# Revit family: MADEL_DAMPER_AIR VOLUME CONTROL_SQR_tarifa
name_source: partatom
category: Accesorios de conductos
revit_build: Autodesk Revit 2015 (Build: 20140606_1530(x64)
units: mm (PartAtom-declared; Revit-internal decimal feet)

## types (230) — shared parameters
BIMETRICAL = http://www.bimetrical.com
BIMETRICAL Category = Damper
Comentarios de tipo = The SQR series damper are designed to be used for altering the flow volume rate and pressure in air-conditioning, ventilation and heating systems. Opposed blades of 100 mm.
Descripción = MADEL_Air volume dampers for rectangular ducts
Fabricante = MADEL
Family Version = 1.0
IfcExportAs = IfcDamperType
IfcExportType = IfcDamperType
Imagen de tipo = <Ninguno>
Material Damper = <Por categoría>
Review Date = 11/2016
Revit Version = Revit 2015 - English
URL = http://www.madel.com
Vmax = 7.0 m/s
Vmed = 4.0 m/s
Vmin = 1.0 m/s
b_factor = -0.69
c_factor = -6.9395
m_factor = 2.16
n_factor = 28.867

## per-type parameters (varying)
| type | Afree | H | L | Modelo | Nº  Blades | Product Size | Q max | Q min |
| SQR-EH 2000x1000 | 1.9603 m² | 1000 mm  [stored 3.28084 ft] | 2000 mm  [stored 6.56168 ft] | SQR-EH 2000x1000 | 20 | 2000x1000 | 49,398 m³/h | 7,057 m³/h |
| SQR-EH 2000x900 | 1.7642 m² | 900 mm  [stored 2.95276 ft] | 2000 mm  [stored 6.56168 ft] | SQR-EH 2000x900 | 18 | 2000x900 | 44,458 m³/h | 6,351 m³/h |
| SQR-EH 2000x800 | 1.5682 m² | 800 mm  [stored 2.62467 ft] | 2000 mm  [stored 6.56168 ft] | SQR-EH 2000x800 | 16 | 2000x800 | 39,519 m³/h | 5,646 m³/h |
| SQR-EH 2000x700 | 1.3722 m² | 700 mm  [stored 2.29659 ft] | 2000 mm  [stored 6.56168 ft] | SQR-EH 2000x700 | 14 | 2000x700 | 34,579 m³/h | 4,940 m³/h |
| SQR-EH 2000x600 | 1.1762 m² | 600 mm | 2000 mm  [stored 6.56168 ft] | SQR-EH 2000x600 | 12 | 2000x600 | 29,639 m³/h | 4,234 m³/h |
| SQR-EH 2000x500 | 0.9801 m² | 500 mm  [stored 1.64042 ft] | 2000 mm  [stored 6.56168 ft] | SQR-EH 2000x500 | 10 | 2000x500 | 24,699 m³/h | 3,528 m³/h |
| SQR-EH 2000x400 | 0.7841 m² | 400 mm  [stored 1.31234 ft] | 2000 mm  [stored 6.56168 ft] | SQR-EH 2000x400 | 8 | 2000x400 | 19,759 m³/h | 2,823 m³/h |
| SQR-EH 2000x300 | 0.5881 m² | 300 mm | 2000 mm  [stored 6.56168 ft] | SQR-EH 2000x300 | 6 | 2000x300 | 14,819 m³/h | 2,117 m³/h |
| SQR-EH 2000x250 | 0.4921 m² | 250 mm  [stored 0.82021 ft] | 2000 mm  [stored 6.56168 ft] | SQR-EH 2000x250 | 4 | 2000x250 | 12,400 m³/h | 1,771 m³/h |
| SQR-EH 2000x200 | 0.3921 m² | 200 mm  [stored 0.656168 ft] | 2000 mm  [stored 6.56168 ft] | SQR-EH 2000x200 | 4 | 2000x200 | 9,880 m³/h | 1,411 m³/h |
| SQR-EH 2000x150 | 0.2960 m² | 150 mm | 2000 mm  [stored 6.56168 ft] | SQR-EH 2000x150 | 2 | 2000x150 | 7,460 m³/h | 1,066 m³/h |
| SQR-EH 2000x100 | 0.1960 m² | 100 mm  [stored 0.328084 ft] | 2000 mm  [stored 6.56168 ft] | SQR-EH 2000x100 | 2 | 2000x100 | 4,940 m³/h | 706 m³/h |
| SQR-EH 1800x1000 | 1.7643 m² | 1000 mm  [stored 3.28084 ft] | 1800 mm | SQR-EH 1800x1000 | 20 | 1800x1000 | 44,459 m³/h | 6,351 m³/h |
| SQR-EH 1800x900 | 1.5878 m² | 900 mm  [stored 2.95276 ft] | 1800 mm | SQR-EH 1800x900 | 18 | 1800x900 | 40,013 m³/h | 5,716 m³/h |
| SQR-EH 1800x800 | 1.4114 m² | 800 mm  [stored 2.62467 ft] | 1800 mm | SQR-EH 1800x800 | 16 | 1800x800 | 35,567 m³/h | 5,081 m³/h |
| SQR-EH 1800x700 | 1.2350 m² | 700 mm  [stored 2.29659 ft] | 1800 mm | SQR-EH 1800x700 | 14 | 1800x700 | 31,121 m³/h | 4,446 m³/h |
| SQR-EH 1800x600 | 1.0586 m² | 600 mm | 1800 mm | SQR-EH 1800x600 | 12 | 1800x600 | 26,675 m³/h | 3,811 m³/h |
| SQR-EH 1800x500 | 0.8821 m² | 500 mm  [stored 1.64042 ft] | 1800 mm | SQR-EH 1800x500 | 10 | 1800x500 | 22,230 m³/h | 3,176 m³/h |
| SQR-EH 1800x400 | 0.7057 m² | 400 mm  [stored 1.31234 ft] | 1800 mm | SQR-EH 1800x400 | 8 | 1800x400 | 17,784 m³/h | 2,541 m³/h |
| SQR-EH 1800x300 | 0.5293 m² | 300 mm | 1800 mm | SQR-EH 1800x300 | 6 | 1800x300 | 13,338 m³/h | 1,905 m³/h |
| SQR-EH 1800x250 | 0.4429 m² | 250 mm  [stored 0.82021 ft] | 1800 mm | SQR-EH 1800x250 | 4 | 1800x250 | 11,160 m³/h | 1,594 m³/h |
| SQR-EH 1800x200 | 0.3529 m² | 200 mm  [stored 0.656168 ft] | 1800 mm | SQR-EH 1800x200 | 4 | 1800x200 | 8,892 m³/h | 1,270 m³/h |
| SQR-EH 1800x150 | 0.2664 m² | 150 mm | 1800 mm | SQR-EH 1800x150 | 2 | 1800x150 | 6,714 m³/h | 959 m³/h |
| SQR-EH 1800x100 | 0.1764 m² | 100 mm  [stored 0.328084 ft] | 1800 mm | SQR-EH 1800x100 | 2 | 1800x100 | 4,446 m³/h | 635 m³/h |
| SQR-EH 1600x1000 | 1.5683 m² | 1000 mm  [stored 3.28084 ft] | 1600 mm | SQR-EH 1600x1000 | 20 | 1600x1000 | 39,520 m³/h | 5,646 m³/h |
| SQR-EH 1600x900 | 1.4114 m² | 900 mm  [stored 2.95276 ft] | 1600 mm | SQR-EH 1600x900 | 18 | 1600x900 | 35,568 m³/h | 5,081 m³/h |
| SQR-EH 1600x800 | 1.2546 m² | 800 mm  [stored 2.62467 ft] | 1600 mm | SQR-EH 1600x800 | 16 | 1600x800 | 31,616 m³/h | 4,517 m³/h |
| SQR-EH 1600x700 | 1.0978 m² | 700 mm  [stored 2.29659 ft] | 1600 mm | SQR-EH 1600x700 | 14 | 1600x700 | 27,664 m³/h | 3,952 m³/h |
| SQR-EH 1600x600 | 0.9410 m² | 600 mm | 1600 mm | SQR-EH 1600x600 | 12 | 1600x600 | 23,712 m³/h | 3,387 m³/h |
| SQR-EH 1600x500 | 0.7841 m² | 500 mm  [stored 1.64042 ft] | 1600 mm | SQR-EH 1600x500 | 10 | 1600x500 | 19,760 m³/h | 2,823 m³/h |
| SQR-EH 1600x400 | 0.6273 m² | 400 mm  [stored 1.31234 ft] | 1600 mm | SQR-EH 1600x400 | 8 | 1600x400 | 15,808 m³/h | 2,258 m³/h |
| SQR-EH 1600x300 | 0.4705 m² | 300 mm | 1600 mm | SQR-EH 1600x300 | 6 | 1600x300 | 11,856 m³/h | 1,694 m³/h |
| SQR-EH 1600x250 | 0.3937 m² | 250 mm  [stored 0.82021 ft] | 1600 mm | SQR-EH 1600x250 | 4 | 1600x250 | 9,920 m³/h | 1,417 m³/h |
| SQR-EH 1600x200 | 0.3137 m² | 200 mm  [stored 0.656168 ft] | 1600 mm | SQR-EH 1600x200 | 4 | 1600x200 | 7,904 m³/h | 1,129 m³/h |
| SQR-EH 1600x150 | 0.2368 m² | 150 mm | 1600 mm | SQR-EH 1600x150 | 2 | 1600x150 | 5,968 m³/h | 853 m³/h |
| SQR-EH 1600x100 | 0.1568 m² | 100 mm  [stored 0.328084 ft] | 1600 mm | SQR-EH 1600x100 | 2 | 1600x100 | 3,952 m³/h | 565 m³/h |
| SQR-EH 1400x1000 | 1.3723 m² | 1000 mm  [stored 3.28084 ft] | 1400 mm  [stored 4.59318 ft] | SQR-EH 1400x1000 | 20 | 1400x1000 | 34,581 m³/h | 4,940 m³/h |
| SQR-EH 1400x900 | 1.2350 m² | 900 mm  [stored 2.95276 ft] | 1400 mm  [stored 4.59318 ft] | SQR-EH 1400x900 | 18 | 1400x900 | 31,123 m³/h | 4,446 m³/h |
| SQR-EH 1400x800 | 1.0978 m² | 800 mm  [stored 2.62467 ft] | 1400 mm  [stored 4.59318 ft] | SQR-EH 1400x800 | 16 | 1400x800 | 27,665 m³/h | 3,952 m³/h |
| SQR-EH 1400x700 | 0.9606 m² | 700 mm  [stored 2.29659 ft] | 1400 mm  [stored 4.59318 ft] | SQR-EH 1400x700 | 14 | 1400x700 | 24,206 m³/h | 3,458 m³/h |
| SQR-EH 1400x600 | 0.8234 m² | 600 mm | 1400 mm  [stored 4.59318 ft] | SQR-EH 1400x600 | 12 | 1400x600 | 20,748 m³/h | 2,964 m³/h |
| SQR-EH 1400x500 | 0.6861 m² | 500 mm  [stored 1.64042 ft] | 1400 mm  [stored 4.59318 ft] | SQR-EH 1400x500 | 10 | 1400x500 | 17,290 m³/h | 2,470 m³/h |
| SQR-EH 1400x400 | 0.5489 m² | 400 mm  [stored 1.31234 ft] | 1400 mm  [stored 4.59318 ft] | SQR-EH 1400x400 | 8 | 1400x400 | 13,832 m³/h | 1,976 m³/h |
| SQR-EH 1400x300 | 0.4117 m² | 300 mm | 1400 mm  [stored 4.59318 ft] | SQR-EH 1400x300 | 6 | 1400x300 | 10,374 m³/h | 1,482 m³/h |
| SQR-EH 1400x250 | 0.3445 m² | 250 mm  [stored 0.82021 ft] | 1400 mm  [stored 4.59318 ft] | SQR-EH 1400x250 | 4 | 1400x250 | 8,680 m³/h | 1,240 m³/h |
| SQR-EH 1400x200 | 0.2745 m² | 200 mm  [stored 0.656168 ft] | 1400 mm  [stored 4.59318 ft] | SQR-EH 1400x200 | 4 | 1400x200 | 6,916 m³/h | 988 m³/h |
| SQR-EH 1400x150 | 0.2072 m² | 150 mm | 1400 mm  [stored 4.59318 ft] | SQR-EH 1400x150 | 2 | 1400x150 | 5,222 m³/h | 746 m³/h |
| SQR-EH 1400x100 | 0.1372 m² | 100 mm  [stored 0.328084 ft] | 1400 mm  [stored 4.59318 ft] | SQR-EH 1400x100 | 2 | 1400x100 | 3,458 m³/h | 494 m³/h |
| SQR-EH 1200x1000 | 1.1881 m² | 1000 mm  [stored 3.28084 ft] | 1200 mm | SQR-EH 1200x1000 | 10 | 1200x1000 | 29,941 m³/h | 4,277 m³/h |
| SQR-EH 1200x900 | 1.0693 m² | 900 mm  [stored 2.95276 ft] | 1200 mm | SQR-EH 1200x900 | 9 | 1200x900 | 26,947 m³/h | 3,850 m³/h |
| SQR-EH 1200x800 | 0.9505 m² | 800 mm  [stored 2.62467 ft] | 1200 mm | SQR-EH 1200x800 | 8 | 1200x800 | 23,953 m³/h | 3,422 m³/h |
| SQR-EH 1200x700 | 0.8317 m² | 700 mm  [stored 2.29659 ft] | 1200 mm | SQR-EH 1200x700 | 7 | 1200x700 | 20,959 m³/h | 2,994 m³/h |
| SQR-EH 1200x600 | 0.7129 m² | 600 mm | 1200 mm | SQR-EH 1200x600 | 6 | 1200x600 | 17,964 m³/h | 2,566 m³/h |
| SQR-EH 1200x500 | 0.5941 m² | 500 mm  [stored 1.64042 ft] | 1200 mm | SQR-EH 1200x500 | 5 | 1200x500 | 14,970 m³/h | 2,139 m³/h |
| SQR-EH 1200x400 | 0.4753 m² | 400 mm  [stored 1.31234 ft] | 1200 mm | SQR-EH 1200x400 | 4 | 1200x400 | 11,976 m³/h | 1,711 m³/h |
| SQR-EH 1200x300 | 0.3564 m² | 300 mm | 1200 mm | SQR-EH 1200x300 | 3 | 1200x300 | 8,982 m³/h | 1,283 m³/h |
| SQR-EH 1200x250 | 0.2976 m² | 250 mm  [stored 0.82021 ft] | 1200 mm | SQR-EH 1200x250 | 2 | 1200x250 | 7,500 m³/h | 1,071 m³/h |
| SQR-EH 1200x200 | 0.2376 m² | 200 mm  [stored 0.656168 ft] | 1200 mm | SQR-EH 1200x200 | 2 | 1200x200 | 5,988 m³/h | 855 m³/h |
| SQR-EH 1200x150 | 0.1788 m² | 150 mm | 1200 mm | SQR-EH 1200x150 | 1 | 1200x150 | 4,506 m³/h | 644 m³/h |
| SQR-EH 1200x100 | 0.1188 m² | 100 mm  [stored 0.328084 ft] | 1200 mm | SQR-EH 1200x100 | 1 | 1200x100 | 2,994 m³/h | 428 m³/h |
| SQR-EH 1100x1000 | 1.0891 m² | 1000 mm  [stored 3.28084 ft] | 1100 mm | SQR-EH 1100x1000 | 10 | 1100x1000 | 27,446 m³/h | 3,921 m³/h |
| SQR-EH 1100x900 | 0.9802 m² | 900 mm  [stored 2.95276 ft] | 1100 mm | SQR-EH 1100x900 | 9 | 1100x900 | 24,701 m³/h | 3,529 m³/h |
| SQR-EH 1100x800 | 0.8713 m² | 800 mm  [stored 2.62467 ft] | 1100 mm | SQR-EH 1100x800 | 8 | 1100x800 | 21,957 m³/h | 3,137 m³/h |
| SQR-EH 1100x700 | 0.7624 m² | 700 mm  [stored 2.29659 ft] | 1100 mm | SQR-EH 1100x700 | 7 | 1100x700 | 19,212 m³/h | 2,745 m³/h |
| SQR-EH 1100x600 | 0.6535 m² | 600 mm | 1100 mm | SQR-EH 1100x600 | 6 | 1100x600 | 16,468 m³/h | 2,353 m³/h |
| SQR-EH 1100x500 | 0.5446 m² | 500 mm  [stored 1.64042 ft] | 1100 mm | SQR-EH 1100x500 | 5 | 1100x500 | 13,723 m³/h | 1,960 m³/h |
| SQR-EH 1100x400 | 0.4357 m² | 400 mm  [stored 1.31234 ft] | 1100 mm | SQR-EH 1100x400 | 4 | 1100x400 | 10,978 m³/h | 1,568 m³/h |
| SQR-EH 1100x300 | 0.3267 m² | 300 mm | 1100 mm | SQR-EH 1100x300 | 3 | 1100x300 | 8,234 m³/h | 1,176 m³/h |
| SQR-EH 1100x250 | 0.2728 m² | 250 mm  [stored 0.82021 ft] | 1100 mm | SQR-EH 1100x250 | 2 | 1100x250 | 6,875 m³/h | 982 m³/h |
| SQR-EH 1100x200 | 0.2178 m² | 200 mm  [stored 0.656168 ft] | 1100 mm | SQR-EH 1100x200 | 2 | 1100x200 | 5,489 m³/h | 784 m³/h |
| SQR-EH 1100x150 | 0.1639 m² | 150 mm | 1100 mm | SQR-EH 1100x150 | 1 | 1100x150 | 4,131 m³/h | 590 m³/h |
| SQR-EH 1100x100 | 0.1089 m² | 100 mm  [stored 0.328084 ft] | 1100 mm | SQR-EH 1100x100 | 1 | 1100x100 | 2,745 m³/h | 392 m³/h |
| SQR-EH 1000x1000 | 0.9901 m² | 1000 mm  [stored 3.28084 ft] | 1000 mm  [stored 3.28084 ft] | SQR-EH 1000x1000 | 10 | 1000x1000 | 24,951 m³/h | 3,564 m³/h |
| SQR-EH 1000x900 | 0.8911 m² | 900 mm  [stored 2.95276 ft] | 1000 mm  [stored 3.28084 ft] | SQR-EH 1000x900 | 9 | 1000x900 | 22,456 m³/h | 3,208 m³/h |
| SQR-EH 1000x800 | 0.7921 m² | 800 mm  [stored 2.62467 ft] | 1000 mm  [stored 3.28084 ft] | SQR-EH 1000x800 | 8 | 1000x800 | 19,961 m³/h | 2,852 m³/h |
| SQR-EH 1000x700 | 0.6931 m² | 700 mm  [stored 2.29659 ft] | 1000 mm  [stored 3.28084 ft] | SQR-EH 1000x700 | 7 | 1000x700 | 17,466 m³/h | 2,495 m³/h |
| SQR-EH 1000x600 | 0.5941 m² | 600 mm | 1000 mm  [stored 3.28084 ft] | SQR-EH 1000x600 | 6 | 1000x600 | 14,971 m³/h | 2,139 m³/h |
| SQR-EH 1000x500 | 0.4951 m² | 500 mm  [stored 1.64042 ft] | 1000 mm  [stored 3.28084 ft] | SQR-EH 1000x500 | 5 | 1000x500 | 12,476 m³/h | 1,782 m³/h |
| SQR-EH 1000x400 | 0.3961 m² | 400 mm  [stored 1.31234 ft] | 1000 mm  [stored 3.28084 ft] | SQR-EH 1000x400 | 4 | 1000x400 | 9,980 m³/h | 1,426 m³/h |
| SQR-EH 1000x300 | 0.2970 m² | 300 mm | 1000 mm  [stored 3.28084 ft] | SQR-EH 1000x300 | 3 | 1000x300 | 7,485 m³/h | 1,069 m³/h |
| SQR-EH 1000x250 | 0.2480 m² | 250 mm  [stored 0.82021 ft] | 1000 mm  [stored 3.28084 ft] | SQR-EH 1000x250 | 2 | 1000x250 | 6,250 m³/h | 893 m³/h |
| SQR-EH 1000x200 | 0.1980 m² | 200 mm  [stored 0.656168 ft] | 1000 mm  [stored 3.28084 ft] | SQR-EH 1000x200 | 2 | 1000x200 | 4,990 m³/h | 713 m³/h |
| SQR-EH 1000x150 | 0.1490 m² | 150 mm | 1000 mm  [stored 3.28084 ft] | SQR-EH 1000x150 | 1 | 1000x150 | 3,755 m³/h | 536 m³/h |
| SQR-EH 1000x100 | 0.0990 m² | 100 mm  [stored 0.328084 ft] | 1000 mm  [stored 3.28084 ft] | SQR-EH 1000x100 | 1 | 1000x100 | 2,495 m³/h | 356 m³/h |
| SQR-EV 1000x900 | 0.8911 m² | 1000 mm  [stored 3.28084 ft] | 900 mm  [stored 2.95276 ft] | SQR-EV 1000x900 | 10 | 900x1000 | 22,456 m³/h | 3,208 m³/h |
| SQR-EH 900x900 | 0.8020 m² | 900 mm  [stored 2.95276 ft] | 900 mm  [stored 2.95276 ft] | SQR-EH 900x900 | 9 | 900x900 | 20,211 m³/h | 2,887 m³/h |
| SQR-EH 900x800 | 0.7129 m² | 800 mm  [stored 2.62467 ft] | 900 mm  [stored 2.95276 ft] | SQR-EH 900x800 | 8 | 900x800 | 17,965 m³/h | 2,566 m³/h |
| SQR-EH 900x700 | 0.6238 m² | 700 mm  [stored 2.29659 ft] | 900 mm  [stored 2.95276 ft] | SQR-EH 900x700 | 7 | 900x700 | 15,719 m³/h | 2,246 m³/h |
| SQR-EH 900x500 | 0.4456 m² | 500 mm  [stored 1.64042 ft] | 900 mm  [stored 2.95276 ft] | SQR-EH 900x500 | 5 | 900x500 | 11,228 m³/h | 1,604 m³/h |
| SQR-EH 900x400 | 0.3565 m² | 400 mm  [stored 1.31234 ft] | 900 mm  [stored 2.95276 ft] | SQR-EH 900x400 | 4 | 900x400 | 8,983 m³/h | 1,283 m³/h |
| SQR-EH 900x300 | 0.2673 m² | 300 mm | 900 mm  [stored 2.95276 ft] | SQR-EH 900x300 | 3 | 900x300 | 6,737 m³/h | 962 m³/h |
| SQR-EH 900x250 | 0.2232 m² | 250 mm  [stored 0.82021 ft] | 900 mm  [stored 2.95276 ft] | SQR-EH 900x250 | 2 | 900x250 | 5,625 m³/h | 804 m³/h |
| SQR-EH 900x200 | 0.1782 m² | 200 mm  [stored 0.656168 ft] | 900 mm  [stored 2.95276 ft] | SQR-EH 900x200 | 2 | 900x200 | 4,491 m³/h | 642 m³/h |
| SQR-EH 900x150 | 0.1341 m² | 150 mm | 900 mm  [stored 2.95276 ft] | SQR-EH 900x150 | 1 | 900x150 | 3,380 m³/h | 483 m³/h |
| SQR-EH 900x100 | 0.0891 m² | 100 mm  [stored 0.328084 ft] | 900 mm  [stored 2.95276 ft] | SQR-EH 900x100 | 1 | 900x100 | 2,246 m³/h | 321 m³/h |
| SQR-EV 1000x800 | 0.7921 m² | 1000 mm  [stored 3.28084 ft] | 800 mm  [stored 2.62467 ft] | SQR-EV 1000x800 | 10 | 800x1000 | 19,962 m³/h | 2,852 m³/h |
| SQR-EV 900x800 | 0.7129 m² | 900 mm  [stored 2.95276 ft] | 800 mm  [stored 2.62467 ft] | SQR-EV 900x800 | 9 | 800x900 | 17,965 m³/h | 2,566 m³/h |
| SQR-EV 850x800 | 0.6737 m² | 850 mm  [stored 2.78871 ft] | 800 mm  [stored 2.62467 ft] | SQR-EV 850x800 | 8 | 800x850 | 16,977 m³/h | 2,425 m³/h |
| SQR-EH 800x800 | 0.6337 m² | 800 mm  [stored 2.62467 ft] | 800 mm  [stored 2.62467 ft] | SQR-EH 800x800 | 8 | 800x800 | 15,969 m³/h | 2,281 m³/h |
| SQR-EH 800x700 | 0.5545 m² | 700 mm  [stored 2.29659 ft] | 800 mm  [stored 2.62467 ft] | SQR-EH 800x700 | 7 | 800x700 | 13,973 m³/h | 1,996 m³/h |
| SQR-EH 800x600 | 0.4753 m² | 600 mm | 800 mm  [stored 2.62467 ft] | SQR-EH 800x600 | 6 | 800x600 | 11,977 m³/h | 1,711 m³/h |
| SQR-EH 800x500 | 0.3961 m² | 500 mm  [stored 1.64042 ft] | 800 mm  [stored 2.62467 ft] | SQR-EH 800x500 | 5 | 800x500 | 9,981 m³/h | 1,426 m³/h |
| SQR-EH 800x400 | 0.3169 m² | 400 mm  [stored 1.31234 ft] | 800 mm  [stored 2.62467 ft] | SQR-EH 800x400 | 4 | 800x400 | 7,985 m³/h | 1,141 m³/h |
| SQR-EH 800x300 | 0.2376 m² | 300 mm | 800 mm  [stored 2.62467 ft] | SQR-EH 800x300 | 3 | 800x300 | 5,988 m³/h | 855 m³/h |
| SQR-EH 800x250 | 0.1984 m² | 250 mm  [stored 0.82021 ft] | 800 mm  [stored 2.62467 ft] | SQR-EH 800x250 | 2 | 800x250 | 5,000 m³/h | 714 m³/h |
| SQR-EH 800x200 | 0.1584 m² | 200 mm  [stored 0.656168 ft] | 800 mm  [stored 2.62467 ft] | SQR-EH 800x200 | 2 | 800x200 | 3,992 m³/h | 570 m³/h |
| SQR-EH 800x150 | 0.1192 m² | 150 mm | 800 mm  [stored 2.62467 ft] | SQR-EH 800x150 | 1 | 800x150 | 3,004 m³/h | 429 m³/h |
| SQR-EH 800x100 | 0.0792 m² | 100 mm  [stored 0.328084 ft] | 800 mm  [stored 2.62467 ft] | SQR-EH 800x100 | 1 | 800x100 | 1,996 m³/h | 285 m³/h |
| SQR-EH 700x700 | 0.4852 m² | 700 mm  [stored 2.29659 ft] | 700 mm  [stored 2.29659 ft] | SQR-EH 700x700 | 7 | 700x700 | 12,227 m³/h | 1,747 m³/h |
| SQR-EH 700x600 | 0.4159 m² | 600 mm | 700 mm  [stored 2.29659 ft] | SQR-EH 700x600 | 6 | 700x600 | 10,480 m³/h | 1,497 m³/h |
| SQR-EH 700x500 | 0.3466 m² | 500 mm  [stored 1.64042 ft] | 700 mm  [stored 2.29659 ft] | SQR-EH 700x500 | 5 | 700x500 | 8,733 m³/h | 1,248 m³/h |
| SQR-EH 700x400 | 0.2773 m² | 400 mm  [stored 1.31234 ft] | 700 mm  [stored 2.29659 ft] | SQR-EH 700x400 | 4 | 700x400 | 6,987 m³/h | 998 m³/h |
| SQR-EH 700x300 | 0.2079 m² | 300 mm | 700 mm  [stored 2.29659 ft] | SQR-EH 700x300 | 3 | 700x300 | 5,240 m³/h | 749 m³/h |
| SQR-EH 700x250 | 0.1736 m² | 250 mm  [stored 0.82021 ft] | 700 mm  [stored 2.29659 ft] | SQR-EH 700x250 | 2 | 700x250 | 4,375 m³/h | 625 m³/h |
| SQR-EH 700x200 | 0.1386 m² | 200 mm  [stored 0.656168 ft] | 700 mm  [stored 2.29659 ft] | SQR-EH 700x200 | 2 | 700x200 | 3,493 m³/h | 499 m³/h |
| SQR-EH 700x150 | 0.1043 m² | 150 mm | 700 mm  [stored 2.29659 ft] | SQR-EH 700x150 | 1 | 700x150 | 2,629 m³/h | 376 m³/h |
| SQR-EH 700x100 | 0.0693 m² | 100 mm  [stored 0.328084 ft] | 700 mm  [stored 2.29659 ft] | SQR-EH 700x100 | 1 | 700x100 | 1,747 m³/h | 250 m³/h |
| SQR-EH 600x600 | 0.3565 m² | 600 mm | 600 mm | SQR-EH 600x600 | 6 | 600x600 | 8,983 m³/h | 1,283 m³/h |
| SQR-EH 600x500 | 0.2971 m² | 500 mm  [stored 1.64042 ft] | 600 mm | SQR-EH 600x500 | 5 | 600x500 | 7,486 m³/h | 1,069 m³/h |
| SQR-EH 600x400 | 0.2377 m² | 400 mm  [stored 1.31234 ft] | 600 mm | SQR-EH 600x400 | 4 | 600x400 | 5,989 m³/h | 856 m³/h |
| SQR-EH 600x300 | 0.1782 m² | 300 mm | 600 mm | SQR-EH 600x300 | 3 | 600x300 | 4,492 m³/h | 642 m³/h |
| SQR-EH 600x250 | 0.1488 m² | 250 mm  [stored 0.82021 ft] | 600 mm | SQR-EH 600x250 | 2 | 600x250 | 3,750 m³/h | 536 m³/h |
| SQR-EH 600x200 | 0.1188 m² | 200 mm  [stored 0.656168 ft] | 600 mm | SQR-EH 600x200 | 2 | 600x200 | 2,994 m³/h | 428 m³/h |
| SQR-EH 600x150 | 0.0894 m² | 150 mm | 600 mm | SQR-EH 600x150 | 1 | 600x150 | 2,253 m³/h | 322 m³/h |
| SQR-EH 600x100 | 0.0594 m² | 100 mm  [stored 0.328084 ft] | 600 mm | SQR-EH 600x100 | 1 | 600x100 | 1,497 m³/h | 214 m³/h |
| SQR-EH 500x500 | 0.2476 m² | 500 mm  [stored 1.64042 ft] | 500 mm  [stored 1.64042 ft] | SQR-EH 500x500 | 5 | 500x500 | 6,239 m³/h | 891 m³/h |
| SQR-EH 500x400 | 0.1981 m² | 400 mm  [stored 1.31234 ft] | 500 mm  [stored 1.64042 ft] | SQR-EH 500x400 | 4 | 500x400 | 4,991 m³/h | 713 m³/h |
| SQR-EH 500x300 | 0.1485 m² | 300 mm | 500 mm  [stored 1.64042 ft] | SQR-EH 500x300 | 3 | 500x300 | 3,743 m³/h | 535 m³/h |
| SQR-EH 500x250 | 0.1240 m² | 250 mm  [stored 0.82021 ft] | 500 mm  [stored 1.64042 ft] | SQR-EH 500x250 | 2 | 500x250 | 3,125 m³/h | 446 m³/h |
| SQR-EH 500x200 | 0.0990 m² | 200 mm  [stored 0.656168 ft] | 500 mm  [stored 1.64042 ft] | SQR-EH 500x200 | 2 | 500x200 | 2,495 m³/h | 356 m³/h |
| SQR-EH 500x150 | 0.0745 m² | 150 mm | 500 mm  [stored 1.64042 ft] | SQR-EH 500x150 | 1 | 500x150 | 1,878 m³/h | 268 m³/h |
| SQR-EH 500x100 | 0.0495 m² | 100 mm  [stored 0.328084 ft] | 500 mm  [stored 1.64042 ft] | SQR-EH 500x100 | 1 | 500x100 | 1,248 m³/h | 178 m³/h |
| SQR-EH 400x400 | 0.1585 m² | 400 mm  [stored 1.31234 ft] | 400 mm  [stored 1.31234 ft] | SQR-EH 400x400 | 4 | 400x400 | 3,993 m³/h | 570 m³/h |
| SQR-EH 400x300 | 0.1188 m² | 300 mm | 400 mm  [stored 1.31234 ft] | SQR-EH 400x300 | 3 | 400x300 | 2,995 m³/h | 428 m³/h |
| SQR-EH 400x250 | 0.0992 m² | 250 mm  [stored 0.82021 ft] | 400 mm  [stored 1.31234 ft] | SQR-EH 400x250 | 2 | 400x250 | 2,500 m³/h | 357 m³/h |
| SQR-EH 400x200 | 0.0792 m² | 200 mm  [stored 0.656168 ft] | 400 mm  [stored 1.31234 ft] | SQR-EH 400x200 | 2 | 400x200 | 1,996 m³/h | 285 m³/h |
| SQR-EH 400x150 | 0.0596 m² | 150 mm | 400 mm  [stored 1.31234 ft] | SQR-EH 400x150 | 1 | 400x150 | 1,502 m³/h | 215 m³/h |
| SQR-EH 400x100 | 0.0396 m² | 100 mm  [stored 0.328084 ft] | 400 mm  [stored 1.31234 ft] | SQR-EH 400x100 | 1 | 400x100 | 998 m³/h | 143 m³/h |
| SQR-EH 300x300 | 0.0891 m² | 300 mm | 300 mm | SQR-EH 300x300 | 3 | 300x300 | 2,246 m³/h | 321 m³/h |
| SQR-EH 300x250 | 0.0744 m² | 250 mm  [stored 0.82021 ft] | 300 mm | SQR-EH 300x250 | 2 | 300x250 | 1,876 m³/h | 268 m³/h |
| SQR-EH 300x200 | 0.0594 m² | 200 mm  [stored 0.656168 ft] | 300 mm | SQR-EH 300x200 | 2 | 300x200 | 1,498 m³/h | 214 m³/h |
| SQR-EH 300x150 | 0.0447 m² | 150 mm | 300 mm | SQR-EH 300x150 | 1 | 300x150 | 1,127 m³/h | 161 m³/h |
| SQR-EH 300x100 | 0.0297 m² | 100 mm  [stored 0.328084 ft] | 300 mm | SQR-EH 300x100 | 1 | 300x100 | 749 m³/h | 107 m³/h |
| SQR-EH 200x200 | 0.0396 m² | 200 mm  [stored 0.656168 ft] | 200 mm  [stored 0.656168 ft] | SQR-EH 200x200 | 2 | 200x200 | 999 m³/h | 143 m³/h |
| SQR-EH 200x150 | 0.0298 m² | 150 mm | 200 mm  [stored 0.656168 ft] | SQR-EH 200x150 | 1 | 200x150 | 751 m³/h | 107 m³/h |
| SQR-EH 200x100 | 0.0198 m² | 100 mm  [stored 0.328084 ft] | 200 mm  [stored 0.656168 ft] | SQR-EH 200x100 | 1 | 200x100 | 499 m³/h | 71 m³/h |
| SQR-EV 1000x200 | 0.1981 m² | 1000 mm  [stored 3.28084 ft] | 200 mm  [stored 0.656168 ft] | SQR-EV 1000x200 | 10 | 200x1000 | 4,993 m³/h | 713 m³/h |
| SQR-EV 900x200 | 0.1783 m² | 900 mm  [stored 2.95276 ft] | 200 mm  [stored 0.656168 ft] | SQR-EV 900x200 | 9 | 200x900 | 4,493 m³/h | 642 m³/h |
| SQR-EV 800x200 | 0.1585 m² | 800 mm  [stored 2.62467 ft] | 200 mm  [stored 0.656168 ft] | SQR-EV 800x200 | 8 | 200x800 | 3,994 m³/h | 571 m³/h |
| SQR-EV 700x200 | 0.1387 m² | 700 mm  [stored 2.29659 ft] | 200 mm  [stored 0.656168 ft] | SQR-EV 700x200 | 7 | 200x700 | 3,495 m³/h | 499 m³/h |
| SQR-EV 600x200 | 0.1189 m² | 600 mm | 200 mm  [stored 0.656168 ft] | SQR-EH 200x600 | 6 | 200x600 | 2,996 m³/h | 428 m³/h |
| SQR-EV 500x200 | 0.0991 m² | 500 mm  [stored 1.64042 ft] | 200 mm  [stored 0.656168 ft] | SQR-EV 500x200 | 5 | 200x500 | 2,496 m³/h | 357 m³/h |
| SQR-EV 400x200 | 0.0793 m² | 400 mm  [stored 1.31234 ft] | 200 mm  [stored 0.656168 ft] | SQR-EV 400x200 | 4 | 200x400 | 1,997 m³/h | 285 m³/h |
| SQR-EV 300x200 | 0.0594 m² | 300 mm | 200 mm  [stored 0.656168 ft] | SQR-EV 300x200 | 3 | 200x300 | 1,498 m³/h | 214 m³/h |
| SQR-EV 1000x300 | 0.2971 m² | 1000 mm  [stored 3.28084 ft] | 300 mm | SQR-EV 1000x300 | 10 | 300x1000 | 7,488 m³/h | 1,070 m³/h |
| SQR-EV 900x300 | 0.2674 m² | 900 mm  [stored 2.95276 ft] | 300 mm | SQR-EV 900x300 | 9 | 300x900 | 6,739 m³/h | 963 m³/h |
| SQR-EV 800x300 | 0.2377 m² | 800 mm  [stored 2.62467 ft] | 300 mm | SQR-EV 800x300 | 8 | 300x800 | 5,990 m³/h | 856 m³/h |
| SQR-EV 700x300 | 0.2080 m² | 700 mm  [stored 2.29659 ft] | 300 mm | SQR-EV 700x300 | 7 | 300x700 | 5,241 m³/h | 749 m³/h |
| SQR-EV 600x300 | 0.1783 m² | 600 mm | 300 mm | SQR-EV 600x300 | 6 | 300x600 | 4,493 m³/h | 642 m³/h |
| SQR-EV 500x300 | 0.1486 m² | 500 mm  [stored 1.64042 ft] | 300 mm | SQR-EV 500x300 | 5 | 300x500 | 3,744 m³/h | 535 m³/h |
| SQR-EV 400x300 | 0.1189 m² | 400 mm  [stored 1.31234 ft] | 300 mm | SQR-EV 400x300 | 4 | 300x400 | 2,995 m³/h | 428 m³/h |
| SQR-EV 1000x400 | 0.3961 m² | 1000 mm  [stored 3.28084 ft] | 400 mm  [stored 1.31234 ft] | SQR-EV 1000x400 | 10 | 400x1000 | 9,982 m³/h | 1,426 m³/h |
| SQR-EV 900x400 | 0.3565 m² | 900 mm  [stored 2.95276 ft] | 400 mm  [stored 1.31234 ft] | SQR-EV 900x400 | 9 | 400x900 | 8,984 m³/h | 1,283 m³/h |
| SQR-EV 800x400 | 0.3169 m² | 800 mm  [stored 2.62467 ft] | 400 mm  [stored 1.31234 ft] | SQR-EV 800x400 | 8 | 400x800 | 7,986 m³/h | 1,141 m³/h |
| SQR-EV 700x400 | 0.2773 m² | 700 mm  [stored 2.29659 ft] | 400 mm  [stored 1.31234 ft] | SQR-EV 700x400 | 7 | 400x700 | 6,988 m³/h | 998 m³/h |
| SQR-EV 600x400 | 0.2377 m² | 600 mm | 400 mm  [stored 1.31234 ft] | SQR-EV 600x400 | 6 | 400x600 | 5,989 m³/h | 856 m³/h |
| SQR-EV 500x400 | 0.1981 m² | 500 mm  [stored 1.64042 ft] | 400 mm  [stored 1.31234 ft] | SQR-EV 500x400 | 5 | 400x500 | 4,991 m³/h | 713 m³/h |
| SQR-EV 1000x500 | 0.4951 m² | 1000 mm  [stored 3.28084 ft] | 500 mm  [stored 1.64042 ft] | SQR-EV 1000x500 | 10 | 500x1000 | 12,477 m³/h | 1,782 m³/h |
| SQR-EV 900x500 | 0.4456 m² | 900 mm  [stored 2.95276 ft] | 500 mm  [stored 1.64042 ft] | SQR-EV 900x500 | 9 | 500x900 | 11,229 m³/h | 1,604 m³/h |
| SQR-EV 800x500 | 0.3961 m² | 800 mm  [stored 2.62467 ft] | 500 mm  [stored 1.64042 ft] | SQR-EV 800x500 | 8 | 500x800 | 9,982 m³/h | 1,426 m³/h |
| SQR-EV 700x500 | 0.3466 m² | 700 mm  [stored 2.29659 ft] | 500 mm  [stored 1.64042 ft] | SQR-EV 700x500 | 7 | 500x700 | 8,734 m³/h | 1,248 m³/h |
| SQR-EV 600x500 | 0.2971 m² | 600 mm | 500 mm  [stored 1.64042 ft] | SQR-EV 600x500 | 6 | 500x600 | 7,486 m³/h | 1,069 m³/h |
| SQR-EV 1000x600 | 0.5941 m² | 1000 mm  [stored 3.28084 ft] | 600 mm | SQR-EV 1000x600 | 10 | 600x1000 | 14,972 m³/h | 2,139 m³/h |
| SQR-EV 900x600 | 0.5347 m² | 900 mm  [stored 2.95276 ft] | 600 mm | SQR-EV 900x600 | 9 | 600x900 | 13,475 m³/h | 1,925 m³/h |
| SQR-EV 800x600 | 0.4753 m² | 800 mm  [stored 2.62467 ft] | 600 mm | SQR-EV 800x600 | 8 | 600x800 | 11,978 m³/h | 1,711 m³/h |
| SQR-EV 700x600 | 0.4159 m² | 700 mm  [stored 2.29659 ft] | 600 mm | SQR-EV 700x600 | 7 | 600x700 | 10,480 m³/h | 1,497 m³/h |
| SQR-EV 1000x700 | 0.6931 m² | 1000 mm  [stored 3.28084 ft] | 700 mm  [stored 2.29659 ft] | SQR-EV 1000x700 | 10 | 700x1000 | 17,467 m³/h | 2,495 m³/h |
| SQR-EV 900x700 | 0.6238 m² | 900 mm  [stored 2.95276 ft] | 700 mm  [stored 2.29659 ft] | SQR-EV 900x700 | 9 | 700x900 | 15,720 m³/h | 2,246 m³/h |
| SQR-EV 800x700 | 0.5545 m² | 800 mm  [stored 2.62467 ft] | 700 mm  [stored 2.29659 ft] | SQR-EV 800x700 | 8 | 700x800 | 13,973 m³/h | 1,996 m³/h |
| SQR-EV 1100x200 | 0.2179 m² | 1100 mm | 200 mm  [stored 0.656168 ft] | SQR-EV 1100x200 | 11 | 200x1100 | 5,492 m³/h | 785 m³/h |
| SQR-EV 1100x300 | 0.3268 m² | 1100 mm | 300 mm | SQR-EV 1100x300 | 11 | 300x1100 | 8,236 m³/h | 1,177 m³/h |
| SQR-EV 1100x400 | 0.4357 m² | 1100 mm | 400 mm  [stored 1.31234 ft] | SQR-EV 1100x400 | 11 | 400x1100 | 10,981 m³/h | 1,569 m³/h |
| SQR-EV 1100x500 | 0.5446 m² | 1100 mm | 500 mm  [stored 1.64042 ft] | SQR-EV 1100x500 | 11 | 500x1100 | 13,725 m³/h | 1,961 m³/h |
| SQR-EV 1100x600 | 0.6535 m² | 1100 mm | 600 mm | SQR-EV 1100x600 | 11 | 600x1100 | 16,469 m³/h | 2,353 m³/h |
| SQR-EV 1100x700 | 0.7624 m² | 1100 mm | 700 mm  [stored 2.29659 ft] | SQR-EV 1100x700 | 11 | 700x1100 | 19,213 m³/h | 2,745 m³/h |
| SQR-EV 1100x800 | 0.8713 m² | 1100 mm | 800 mm  [stored 2.62467 ft] | SQR-EV 1100x800 | 11 | 800x1100 | 21,958 m³/h | 3,137 m³/h |
| SQR-EV 1100x900 | 0.9802 m² | 1100 mm | 900 mm  [stored 2.95276 ft] | SQR-EV 1100x900 | 11 | 900x1100 | 24,702 m³/h | 3,529 m³/h |
| SQR-EV 1100x1000 | 1.0891 m² | 1100 mm | 1000 mm  [stored 3.28084 ft] | SQR-EV 1100x1000 | 11 | 1000x1100 | 27,446 m³/h | 3,921 m³/h |
| SQR-EV 1200x200 | 0.2378 m² | 1200 mm | 200 mm  [stored 0.656168 ft] | SQR-EV 1200x200 | 12 | 200x1200 | 5,991 m³/h | 856 m³/h |
| SQR-EV 1200x300 | 0.3566 m² | 1200 mm | 300 mm | SQR-EV 1200x300 | 12 | 300x1200 | 8,985 m³/h | 1,284 m³/h |
| SQR-EV 1200x400 | 0.4754 m² | 1200 mm | 400 mm  [stored 1.31234 ft] | SQR-EV 1200x400 | 12 | 400x1200 | 11,979 m³/h | 1,711 m³/h |
| SQR-EV 1200x500 | 0.5942 m² | 1200 mm | 500 mm  [stored 1.64042 ft] | SQR-EV 1200x500 | 12 | 500x1200 | 14,973 m³/h | 2,139 m³/h |
| SQR-EV 1200x600 | 0.7130 m² | 1200 mm | 600 mm | SQR-EV 1200x600 | 12 | 600x1200 | 17,966 m³/h | 2,567 m³/h |
| SQR-EV 1200x700 | 0.8318 m² | 1200 mm | 700 mm  [stored 2.29659 ft] | SQR-EV 1200x700 | 12 | 700x1200 | 20,960 m³/h | 2,994 m³/h |
| SQR-EV 1200x800 | 0.9506 m² | 1200 mm | 800 mm  [stored 2.62467 ft] | SQR-EV 1200x800 | 12 | 800x1200 | 23,954 m³/h | 3,422 m³/h |
| SQR-EV 1200x900 | 1.0694 m² | 1200 mm | 900 mm  [stored 2.95276 ft] | SQR-EV 1200x900 | 12 | 900x1200 | 26,948 m³/h | 3,850 m³/h |
| SQR-EV 1200x1000 | 1.1882 m² | 1200 mm | 1000 mm  [stored 3.28084 ft] | SQR-EV 1200x1000 | 12 | 1000x1200 | 29,941 m³/h | 4,277 m³/h |
| SQR-EV 1000x100 | 0.0991 m² | 1000 mm  [stored 3.28084 ft] | 100 mm  [stored 0.328084 ft] | SQR-EV 1000x100 | 10 | 100x1000 | 2,498 m³/h | 357 m³/h |
| SQR-EV 1000x150 | 0.1486 m² | 1000 mm  [stored 3.28084 ft] | 150 mm | SQR-EV 1000x150 | 10 | 150x1000 | 3,745 m³/h | 535 m³/h |
| SQR-EV 1000x250 | 0.2476 m² | 1000 mm  [stored 3.28084 ft] | 250 mm  [stored 0.82021 ft] | SQR-EV 1000x250 | 10 | 250x1000 | 6,240 m³/h | 891 m³/h |
| SQR-EV 1200x100 | 0.1190 m² | 1200 mm | 100 mm  [stored 0.328084 ft] | SQR-EV 1200x100 | 12 | 100x1200 | 2,998 m³/h | 428 m³/h |
| SQR-EV 1200x150 | 0.1784 m² | 1200 mm | 150 mm | SQR-EV 1200x150 | 12 | 150x1200 | 4,494 m³/h | 642 m³/h |
| SQR-EV 1200x250 | 0.2972 m² | 1200 mm | 250 mm  [stored 0.82021 ft] | SQR-EV 1200x250 | 12 | 250x1200 | 7,488 m³/h | 1,070 m³/h |
| SQR-EV 200x100 | 0.0198 m² | 200 mm  [stored 0.656168 ft] | 100 mm  [stored 0.328084 ft] | SQR-EV 200x100 | 2 | 100x200 | 500 m³/h | 71 m³/h |
| SQR-EV 200x150 | 0.0297 m² | 200 mm  [stored 0.656168 ft] | 150 mm | SQR-EV 200x150 | 2 | 150x200 | 749 m³/h | 107 m³/h |
| SQR-EV 300x100 | 0.0297 m² | 300 mm | 100 mm  [stored 0.328084 ft] | SQR-EV 300x100 | 3 | 100x300 | 749 m³/h | 107 m³/h |
| SQR-EV 300x150 | 0.0446 m² | 300 mm | 150 mm | SQR-EV 300x150 | 3 | 150x300 | 1,124 m³/h | 161 m³/h |
| SQR-EV 300x250 | 0.0743 m² | 300 mm | 250 mm  [stored 0.82021 ft] | SQR-EV 300x250 | 3 | 250x300 | 1,872 m³/h | 267 m³/h |
| SQR-EV 400x100 | 0.0397 m² | 400 mm  [stored 1.31234 ft] | 100 mm  [stored 0.328084 ft] | SQR-EV 400x100 | 4 | 100x400 | 999 m³/h | 143 m³/h |
| SQR-EV 400x150 | 0.0595 m² | 400 mm  [stored 1.31234 ft] | 150 mm | SQR-EV 400x150 | 4 | 150x400 | 1,498 m³/h | 214 m³/h |
| SQR-EV 400x250 | 0.0991 m² | 400 mm  [stored 1.31234 ft] | 250 mm  [stored 0.82021 ft] | SQR-EV 400x250 | 4 | 250x400 | 2,496 m³/h | 357 m³/h |
| SQR-EV 500x100 | 0.0496 m² | 500 mm  [stored 1.64042 ft] | 100 mm  [stored 0.328084 ft] | SQR-EV 500x100 | 5 | 100x500 | 1,249 m³/h | 178 m³/h |
| SQR-EV 600x100 | 0.0595 m² | 600 mm | 100 mm  [stored 0.328084 ft] | SQR-EV 600x100 | 6 | 100x600 | 1,499 m³/h | 214 m³/h |
| SQR-EV 700x100 | 0.0694 m² | 700 mm  [stored 2.29659 ft] | 100 mm  [stored 0.328084 ft] | SQR-EV 700x100 | 7 | 100x700 | 1,749 m³/h | 250 m³/h |
| SQR-EV 800x100 | 0.0793 m² | 800 mm  [stored 2.62467 ft] | 100 mm  [stored 0.328084 ft] | SQR-EV 800x100 | 8 | 100x800 | 1,998 m³/h | 285 m³/h |
| SQR-EV 900x100 | 0.0892 m² | 900 mm  [stored 2.95276 ft] | 100 mm  [stored 0.328084 ft] | SQR-EV 900x100 | 9 | 100x900 | 2,248 m³/h | 321 m³/h |
| SQR-EV 900x150 | 0.1338 m² | 900 mm  [stored 2.95276 ft] | 150 mm | SQR-EV 900x150 | 9 | 150x900 | 3,371 m³/h | 482 m³/h |
| SQR-EV 800x150 | 0.1189 m² | 800 mm  [stored 2.62467 ft] | 150 mm | SQR-EV 800x150 | 8 | 150x800 | 2,996 m³/h | 428 m³/h |
| SQR-EV 700x150 | 0.1040 m² | 700 mm  [stored 2.29659 ft] | 150 mm | SQR-EV 700x150 | 7 | 150x700 | 2,622 m³/h | 375 m³/h |
| SQR-EV 600x150 | 0.0892 m² | 600 mm | 150 mm | SQR-EV 600x150 | 6 | 150x600 | 2,247 m³/h | 321 m³/h |
| SQR-EV 500x150 | 0.0743 m² | 500 mm  [stored 1.64042 ft] | 150 mm | SQR-EV 500x150 | 5 | 150x500 | 1,873 m³/h | 268 m³/h |
| SQR-EV 500x250 | 0.1238 m² | 500 mm  [stored 1.64042 ft] | 250 mm  [stored 0.82021 ft] | SQR-EV 500x250 | 5 | 250x500 | 3,120 m³/h | 446 m³/h |
| SQR-EV 600x250 | 0.1486 m² | 600 mm | 250 mm  [stored 0.82021 ft] | SQR-EV 600x250 | 6 | 250x600 | 3,744 m³/h | 535 m³/h |
| SQR-EV 700x250 | 0.1733 m² | 700 mm  [stored 2.29659 ft] | 250 mm  [stored 0.82021 ft] | SQR-EV 700x250 | 7 | 250x700 | 4,368 m³/h | 624 m³/h |
| SQR-EV 800x250 | 0.1981 m² | 800 mm  [stored 2.62467 ft] | 250 mm  [stored 0.82021 ft] | SQR-EV 800x250 | 8 | 250x800 | 4,992 m³/h | 713 m³/h |
| SQR-EV 900x250 | 0.2229 m² | 900 mm  [stored 2.95276 ft] | 250 mm  [stored 0.82021 ft] | SQR-EV 900x250 | 9 | 250x900 | 5,616 m³/h | 802 m³/h |
| SQR-EV 1100x100 | 0.1090 m² | 1100 mm | 100 mm  [stored 0.328084 ft] | SQR-EV 1100x100 | 11 | 100x1100 | 2,748 m³/h | 393 m³/h |
| SQR-EV 1100x150 | 0.1635 m² | 1100 mm | 150 mm | SQR-EV 1100x150 | 11 | 150x1100 | 4,120 m³/h | 589 m³/h |
| SQR-EV 1100x250 | 0.2724 m² | 1100 mm | 250 mm  [stored 0.82021 ft] | SQR-EV 1100x250 | 11 | 250x1100 | 6,864 m³/h | 981 m³/h |
| SQR-EH 900x600 | 0.5347 m² | 600 mm | 900 mm  [stored 2.95276 ft] | SQR-EH 900x600 | 6 | 900x600 | 13,474 m³/h | 1,925 m³/h |

note: [stored X ft] marks values corroborated as IEEE doubles in the binary element streams (Revit-internal decimal feet)

## geometry (parser evidence)
native form markers: Blend x4
no freeform markers — native parametric forms only
